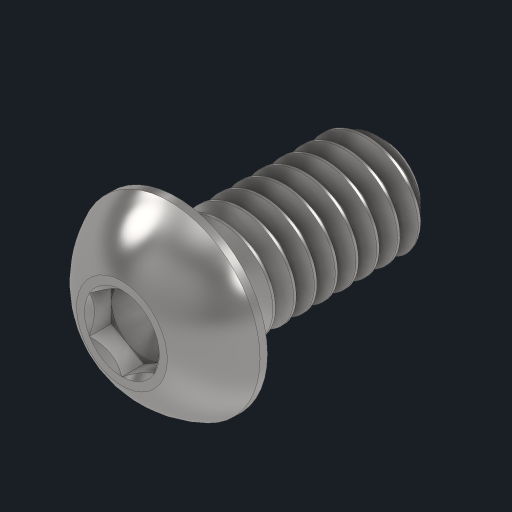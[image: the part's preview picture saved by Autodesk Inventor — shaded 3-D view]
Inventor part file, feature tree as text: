
AUTODESK INVENTOR PART (.ipt)
format: ipt  version: 2024 (Build 280153000, 153)  size: 507,904 bytes
history: native  units: in
note: dims shown in document units (in); Inventor stores cm internally (conversion verified against a paired STEP export)
features: revolve x1
ambient origin geometry x8: Origin, YZ Plane, XZ Plane, XY Plane, X Axis, Y Axis, Z Axis, Center Point
bodies: Solid1 (feature_tree)
feature tree (1):
  revolve  "Revolve2"  [1 undecoded]
note: 1 required parameter value undecoded (feature->parameter linkage not recoverable at this tier; creation-order binding heuristic only, values carry confidence <= 0.55)
